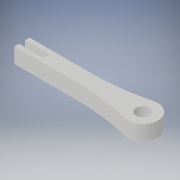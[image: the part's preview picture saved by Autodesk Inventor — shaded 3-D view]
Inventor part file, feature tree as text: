
AUTODESK INVENTOR PART (.ipt)
format: ipt  version: 2019 (Build 230136000, 136)  size: 117,248 bytes
history: native  units: in
note: dims shown in document units (in); Inventor stores cm internally (conversion verified against a paired STEP export)
features: sketch x2, extrude x1, hole x1
ambient origin geometry x8: Origin, YZ Plane, XZ Plane, XY Plane, X Axis, Y Axis, Z Axis, Center Point
bodies: Solid1 (feature_tree)
feature tree (4):
  extrude  "Extrusion1"  Depth=0.1969in
  hole  "Hole1"  [1 undecoded]
  sketch  "Sketch1"  dims[d0=0.1969in d1=0.7874in]
  sketch  "Sketch3"  dims[d2=0.315in d3=0.0787in d4=0.1969in d5=0.0in d6=0.3937in d7=1.1811in d9=0.177in d10=0.2362in d11=0.332in d12=0.0787in d13=0.5635in d14=0.2241in d15=0.8108in d16=0.0394in d17=0.0394in d18=0.0394in d19=0.0059in d20=0.0098in d21=0.0148in d22=0.5635in d23=0.0295in d24=0.8108in d25=0.0025in d26=0.0295in d27=0.0148in]
note: 1 required parameter value undecoded (feature->parameter linkage not recoverable at this tier; creation-order binding heuristic only, values carry confidence <= 0.55)
